# Revit family: KR
name_source: partatom
category: Mechanical Equipment
units: mm (PartAtom-declared; Revit-internal decimal feet)

## family parameters
Always vertical = Yes
Cut with Voids When Loaded = No
Part Type = Normal
Room Calculation Point = No
Round Connector Dimension = Use Diameter
Shared = No
Work Plane-Based = No

## types (6) — shared parameters
Description = 1-fan Evaporator
HEIGHT = 15.91 "
Manufacturer = Krack Corporation
Revit Family Dates = 03/01/2022SV
Type Comments = KR Series 2-Fan Evaporator
URL = www.krack.com
WIDTH = 15.32 "

## per-type parameters (varying)
| type | 1-FAN | 2-FAN | 3-FAN | 4-FAN | 5-FAN | 6-FAN | Copper Pipes | LENGTH | SUPPORT | SUPPORT HING |
| KR2 | No | Yes | No | No | No | No | Copper | 47.13 " | 16.72 " | No |
| KR1 | Yes | No | No | No | No | No | <By Category> | 29.13 " | 8 " | No |
| KR3 | No | No | Yes | No | No | No | Copper | 65.13 " | 25.72 " | No |
| KR4 | No | No | No | Yes | No | No | Copper | 83.13 " | 36 " | Yes |
| KR5 | No | No | No | No | Yes | No | Copper | 101.13 " | 54 " | Yes |
| KR6 | No | No | No | No | No | Yes | Copper | 119.13 " | 54 " | Yes |

note: column(s) folded — value = type name in every type: Model

## geometry (parser evidence)
native form markers: Sweep x12
no freeform markers — native parametric forms only
